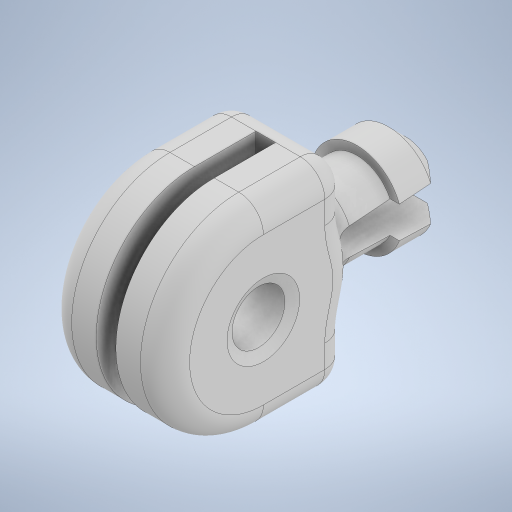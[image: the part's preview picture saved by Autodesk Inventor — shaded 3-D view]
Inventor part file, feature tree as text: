
AUTODESK INVENTOR PART (.ipt)
format: ipt  version: 2023.1 (Build 271208000, 208)  size: 417,792 bytes
history: native  units: mm
features: other x8, extrude x5, projected_geometry x3, chamfer x2, plane x1, loft x1, fillet x1
ambient origin geometry x8: Origin, YZ Plane, XZ Plane, XY Plane, X Axis, Y Axis, Z Axis, Center Point
bodies: Solid1 (feature_tree)
feature tree (21):
  other  "ripple_swivel_clip_v2.ipt"
  extrude  "Clip Base"  Depth=8.0mm
  plane  "Work Plane (Slot Cut)"
  extrude  "Fin Slot Cut"  Depth=3.5mm
  extrude  "Snap Shaft"  Depth=2.15mm
  extrude  "Snap Lip"  Depth=4.8mm TaperAngle=0.0deg
  loft  "Snap Flex Cut"
  chamfer  "Entry Chamfer (Snap Tip)"  Distance=6.5mm
  fillet  "Body Fillets (Clip Base)"  Radius=3.0mm
  extrude  "Hex Nut Slot"  Depth=4.7mm TaperAngle=0.0deg
  chamfer  "Screw Head Chamfer (Outer Face)"  Distance=3.7mm
  other  "Base Profile"
  other  "Fin Slot Layout"
  other  "Shaft Profile"
  projected_geometry  "Projected Loop1"
  other  "Lip Profile"
  projected_geometry  "Projected Loop2"
  other  "Upper Flex Profile"
  projected_geometry  "Projected Loop3"
  other  "Lower Flex Profile"
  other  "Hex Slot Profile"
